# Revit family: QF_ELECTROLUXPROFESSIONAL_1LSN7T_WB6-27_E
name_source: partatom
category: Attrezzature speciali
units: mm (PartAtom-declared; Revit-internal decimal feet)

## family parameters
Basato su piano di lavoro = No
Condiviso = No
Punto di calcolo locali = No
Quota connettore circolare = Usa diametro
Sempre verticale = Sì
Taglio con vuoti quando caricato = No
Tipo di parte = Normale

## types (133) — shared parameters
Cold Water Maximum Pressure = 0.00 psi
Cold Water Minimum Pressure = 0.00 psi
Cold Water Size = 1"
Conn Conduit = Sì
Depth Actual = 1030 mm  [stored 3.37927 ft]
Electrical Remarks = 400 V/3N ph/50/60 Hz
Height Actual = 1620 mm
Hot Water Consumption = 0 GPM
Hot Water Maximum Pressure = 0.00 psi
Hot Water Minimum Pressure = 0.00 psi
Hot Water Size = 1"
Hot Water Temperature = -460 °F
Indirect Waste Size = 1"
Latent Heat Output = 0.0
Length Actual = 1050 mm
Max Overcurrent Protection = 0 A
Min Ckt Ampacity = 0 A
Modello = WB6-27
Phase = 3
Produttore = Electrolux Professional
Sensible Heat Output = 0.0
URL = www.electroluxprofessional.com
Weight = 710
Weight in Pounds = 55.1
zero-valued in all types: Cold Water Connection Height, Gas KW, Hot Water Connection Height, Indirect Waste Connection Height, Prospetto di default, Steam Pounds per Hour

## per-type parameters (varying)
| type | Descrizione | Volts | Watts |
| 9890130043 | WASHER WB6-27 270L 2DOORS RIGHT/RIGHT NO HEATING 380-415/50/60/3 2xCOMPASS PRO 3xWATER 13xLIQ. 2xDRAIN SILVER AIDO TAP A | 415 V | 6200 W |
| 9890130063 | WASHER WB6-27 270L 2DOORS RIGHT/RIGHT EL. 380-415/50/60/3 2xCOMPASS PRO 2xWATER 13xLIQ.+POWDER SILVER AIDO | 415 V | 19500 W |
| 9890130073 | WASHER WB6-27 270L 2DOORS RIGHT/RIGHT EL. 380-415/50/60/3 2xCOMPASS PRO 2xWATER 13xLIQ. SILVER TAP ALARM | 415 V | 19500 W |
| 9890130013 | WASHER WB6-27 270L 2DOORS RIGHT/RIGHT EL. 380-415/50/60/3 2xCOMPASS PRO 2xWATER 13xLIQ. SILVER AIDO IWS TAP ALARM EXP. | 415 V | 19500 W |
| 9890130023 | WASHER WB6-27 270L 2DOORS RIGHT/RIGHT EL. 380-415/50/60/3 2xCOMPASS PRO 2xWATER 13xLIQ. SILVER TAP ALARM EXP. | 415 V | 19500 W |
| 9890130083 | WASHER WB6-27 270L 2DOORS LEFT/LEFT EL. 380-415/50/60/3 COMPASS PRO 2xWATER 13xLIQ. SILVER ALARM | 415 V | 19500 W |
| 9890130093 | WASHER WB6-27 270L 2DOORS RIGHT/RIGHT EL. 380-415/50/60/3 COMPASS PRO 2xWATER 13xLIQ. SILVER TAP ALARM EXP. | 415 V | 19500 W |
| 9890130143 | WASHER WB6-27 270L 2DOORS LEFT/RIGHT EL. 380-415/50/60/3 2xCOMPASS PRO 2xWATER 13xLIQ. SILVER AIDO ALARM | 415 V | 19500 W |
| 9890130046 | WASHER WB6-27 270L 2DOORS RIGHT/RIGHT EL. 380-415/50/60/3 2xCOMPASS PRO 2xWATER 13xLIQ. SILVER AIDO IWS TAP ALARM BMP EX | 415 V | 19500 W |
| 9890130056 | WASHER WB6-27 270L 2DOORS RIGHT/RIGHT EL. 380-415/50/60/3 COMPASS PRO 2xWATER 13xLIQ.+POWDER SST IWS TAP ALARM EXP. | 415 V | 19500 W |
| 9890130103 | WASHER WB6-27 270L 2DOORS LEFT/LEFT EL. 380-415/50/60/3 COMPASS PRO 2xWATER 13xLIQ.+POWDER SILVER EXP. | 415 V | 19500 W |
| 9890130076 | WASHER WB6-27 270L 2DOORS RIGHT/RIGHT EL. 380-415/50/60/3 COMPASS PRO 2xWATER 13xLIQ. SILVER ALARM | 415 V | 19500 W |
| 9890130123 | WASHER WB6-27 270L 2DOORS LEFT/LEFT EL. 380-415/50/60/3 2xCOMPASS PRO 2xWATER 13xLIQ. SILVER | 415 V | 19500 W |
| 9890130016 | WASHER WB6-27 270L 2DOORS RIGHT/RIGHT EL. 380-415/50/60/3 2xCOMPASS PRO 2xWATER 13xLIQ. SILVER | 415 V | 19500 W |
| 9890130133 | WASHER WB6-27 270L 2DOORS RIGHT/RIGHT EL. 380-415/50/60/3 COMPASS PRO 2xWATER 13xLIQ.+POWDER SILVER TAP ALARM | 415 V | 19500 W |
| 9890130006 | WASHER WB6-27 270L 2DOORS RIGHT/RIGHT NO HEATING 380-415/50/60/3 2xCOMPASS PRO 2xWATER 13xLIQ. SILVER ALARM | 415 V | 6200 W |
| 9890130036 | WASHER WB6-27 270L 2DOORS RIGHT/RIGHT NO HEATING 380-415/50/60/3 COMPASS PRO 3xWATER 13xLIQ.+POWDER SILVER | 415 V | 6200 W |
| 9890130026 | WASHER WB6-27 270L 2DOORS RIGHT/RIGHT EL. 230/50/60/3 2xCOMPASS PRO 2xWATER 13xLIQ. SILVER AIDO TAP ALARM EXP. | 230 V | 19500 W |
| 9890130066 | WASHER WB6-27 270L 2DOORS RIGHT/RIGHT EL. 380-415/50/60/3 COMPASS PRO 3xWATER 13xLIQ. SILVER EXP. | 415 V | 19500 W |
| 9890130113 | WASHER WB6-27 270L 2DOORS RIGHT/RIGHT EL. 380-415/50/60/3 COMPASS PRO 2xWATER 13xLIQ. SILVER EXP. | 415 V | 19500 W |
| 9890130086 | WASHER WB6-27 270L 2DOORS LEFT/RIGHT EL. 380-415/50/60/3 2xCOMPASS PRO 3xWATER 13xLIQ.+POWDER SST ALARM EXP. | 415 V | 19500 W |
| 9890130096 | WASHER WB6-27 270L 2DOORS RIGHT/RIGHT EL. 380-415/50/60/3 2xCOMPASS PRO 2xWATER 13xLIQ. SST IWS | 415 V | 19500 W |
| 9890130148 | WASHER WB6-27 270L 2DOORS RIGHT/RIGHT EL. 380-415/50/60/3 COMPASS PRO 3xWATER 13xLIQ. 2xDRAIN SILVER IWS TAP ALARM | 415 V | 19500 W |
| 9890130108 | WASHER WB6-27 270L 2DOORS RIGHT/RIGHT EL. 200/60/3 COMPASS PRO 2xWATER 13xLIQ.+POWDER SST IWS ALARM EXP. | 200 V | 19500 W |
| 9890130118 | WASHER WB6-27 270L 2DOORS RIGHT/RIGHT EL. 208-240/50/60/3 2xCOMPASS PRO 2xWATER 13xLIQ. SILVER TAP ALARM EXP. | 240 V | 19500 W |
| 9890130128 | WASHER WB6-27 270L 2DOORS LEFT/RIGHT EL. 380-415/50/60/3 2xCOMPASS PRO 2xWATER 13xLIQ. SILVER TAP ALARM | 415 V | 19500 W |
| 9890130042 | WASHER WB6-27 270L 2DOORS RIGHT/RIGHT EL. 380-415/50/60/3 COMPASS PRO 2xWATER 13xLIQ.+POWDER SILVER EXP. | 415 V | 19500 W |
| 9890130052 | WASHER WB6-27 270L 2DOORS RIGHT/RIGHT EL. 380-415/50/60/3 2xCOMPASS PRO 2xWATER 13xLIQ.+POWDER SILVER EXP. | 415 V | 19500 W |
| 9890130062 | WASHER WB6-27 270L 2DOORS RIGHT/LEFT EL. 380-415/50/60/3 COMPASS PRO 3xWATER 13xLIQ.+POWDER SILVER EXP. | 415 V | 19500 W |
| 9890130012 | WASHER WB6-27 270L 2DOORS RIGHT/RIGHT EL. 380-415/50/60/3 COMPASS PRO 3xWATER 13xLIQ. SILVER IWS ALARM | 415 V | 19500 W |
| 9890130022 | WASHER WB6-27 270L 2DOORS LEFT/RIGHT EL. 380-415/50/60/3 2xCOMPASS PRO 2xWATER 13xLIQ. SILVER EXP. | 415 V | 19500 W |
| 9890130032 | WASHER WB6-27 270L 2DOORS RIGHT/RIGHT EL. 380-415/50/60/3 2xCOMPASS PRO 2xWATER 13xLIQ. SILVER ALARM | 415 V | 19500 W |
| 9890130082 | WASHER WB6-27 270L 2DOORS LEFT/RIGHT EL. 380-415/50/60/3 COMPASS PRO 2xWATER 13xLIQ. SILVER IWS | 415 V | 19500 W |
| 9890130092 | WASHER WB6-27 270L 2DOORS LEFT/RIGHT EL. 380-415/50/60/3 2xCOMPASS PRO 2xWATER 13xLIQ.+POWDER SILVER ALARM | 415 V | 19500 W |
| 9890130104 | WASHER WB6-27 270L 2DOORS RIGHT/RIGHT EL. 380-415/50/60/3 COMPASS PRO 2xWATER 13xLIQ.+POWDER SILVER EXP. | 415 V | 19500 W |
| 9890130059 | WASHER WB6-27 270L 2DOORS RIGHT/LEFT EL. 380-415/50/60/3 COMPASS PRO 2xWATER 13xLIQ. SILVER EXP. | 415 V | 19500 W |
| 9890130069 | WASHER WB6-27 270L 2DOORS RIGHT/RIGHT EL. 380-415/50/60/3 2xCOMPASS PRO 3xWATER 13xLIQ.+POWDER SILVER AIDO ALARM EXP. | 415 V | 19500 W |
| 9890130134 | WASHER WB6-27 270L 2DOORS RIGHT/RIGHT EL. 380-415/50/60/3 2xCOMPASS PRO 3xWATER 13xLIQ. SILVER AIDO ALARM | 415 V | 19500 W |
| 9890130079 | WASHER WB6-27 270L 2DOORS LEFT/LEFT EL. 380-415/50/60/3 2xCOMPASS PRO 3xWATER 13xLIQ.+POWDER 2xDRAIN SILVER TAP ALARM EX | 415 V | 19500 W |
| 9890130009 | WASHER WB6-27 270L 2DOORS RIGHT/RIGHT EL. 380-415/50/60/3 COMPASS PRO 2xWATER 13xLIQ.+POWDER SILVER EXP. | 415 V | 19500 W |
| 9890130019 | WASHER WB6-27 270L 2DOORS LEFT/RIGHT EL. 380-415/50/60/3 COMPASS PRO 2xWATER 13xLIQ. SILVER | 415 V | 19500 W |
| 9890130029 | WASHER WB6-27 270L 2DOORS RIGHT/RIGHT NO HEATING 380-415/50/60/3 COMPASS PRO 3xWATER 13xLIQ. SILVER | 415 V | 6200 W |
| 9890130039 | WASHER WB6-27 270L 2DOORS LEFT/RIGHT EL. 380-415/50/60/3 COMPASS PRO 2xWATER 13xLIQ.+POWDER SILVER | 415 V | 19500 W |
| 9890130049 | WASHER WB6-27 270L 2DOORS RIGHT/LEFT EL. 380-415/50/60/3 COMPASS PRO 2xWATER 13xLIQ.+POWDER SILVER | 415 V | 19500 W |
| 9890130114 | WASHER WB6-27 270L 2DOORS RIGHT/RIGHT EL. 380-415/50/60/3 2xCOMPASS PRO 2xWATER 13xLIQ.+POWDER SST AIDO ALARM EXP. | 415 V | 19500 W |
| 9890130089 | WASHER WB6-27 270L 2DOORS LEFT/RIGHT EL. 380-415/50/60/3 2xCOMPASS PRO 2xWATER 13xLIQ. SILVER | 415 V | 19500 W |
| 9890130099 | WASHER WB6-27 270L 2DOORS RIGHT/RIGHT EL. 380-415/50/60/3 COMPASS PRO 3xWATER 13xLIQ. SILVER TAP | 415 V | 19500 W |
| 9890130150 | WASHER WB6-27 270L 2DOORS RIGHT/RIGHT EL. 380-415/50/60/3 2xCOMPASS PRO 2xWATER 13xLIQ. SST IWS TAP ALARM BMP EXP. | 415 V | 19500 W |
| 9890130100 | WASHER WB6-27 270L 2DOORS LEFT/RIGHT NO HEATING 380-415/50/60/3 2xCOMPASS PRO 2xWATER 13xLIQ.+POWDER SILVER EXP. | 415 V | 6200 W |
| 9890130055 | WASHER WB6-27 270L 2DOORS RIGHT/RIGHT EL. 380-415/50/60/3 COMPASS PRO 3xWATER 13xLIQ.+POWDER SILVER BMP | 415 V | 19500 W |
| 9890130120 | WASHER WB6-27 270L 2DOORS RIGHT/RIGHT EL. 380-415/50/60/3 2xCOMPASS PRO 2xWATER 13xLIQ. SST AIDO ALARM | 415 V | 19500 W |
| 9890130075 | WASHER WB6-27 270L 2DOORS RIGHT/RIGHT EL. 380-415/50/60/3 2xCOMPASS PRO 2xWATER 13xLIQ. SILVER AIDO IWS ALARM | 415 V | 19500 W |
| 9890130005 | WASHER WB6-27 270L 2DOORS LEFT/RIGHT EL. 380-415/50/60/3 2xCOMPASS PRO 2xWATER 13xLIQ.+POWDER SILVER IWS TAP ALARM EXP. | 415 V | 19500 W |
| 9890130015 | WASHER WB6-27 270L 2DOORS RIGHT/RIGHT EL. 380-415/50/60/3 COMPASS PRO 2xWATER 13xLIQ. SST | 415 V | 19500 W |
| 9890130025 | WASHER WB6-27 270L 2DOORS RIGHT/RIGHT EL. 230/50/60/3 2xCOMPASS PRO 2xWATER 13xLIQ. SILVER TAP ALARM EXP. | 230 V | 19500 W |
| 9890130035 | WASHER WB6-27 270L 2DOORS RIGHT/RIGHT EL. 380-415/50/60/3 2xCOMPASS PRO 2xWATER 13xLIQ. SILVER EXP. | 415 V | 19500 W |
| 9890130110 | WASHER WB6-27 270L 2DOORS RIGHT/RIGHT NO HEATING 380-415/50/60/3 COMPASS PRO 2xWATER 13xLIQ.+POWDER SILVER EXP. | 415 V | 6200 W |
| 9890130085 | WASHER WB6-27 270L 2DOORS LEFT/RIGHT EL. 230/50/60/3 2xCOMPASS PRO 2xWATER 13xLIQ. SILVER TAP ALARM EXP. | 230 V | 19500 W |
| 9890130095 | WASHER WB6-27 270L 2DOORS RIGHT/RIGHT EL. 380-415/50/60/3 COMPASS PRO 3xWATER 13xLIQ. SILVER | 415 V | 19500 W |
| 9890130145 | WASHER WB6-27 270L 2DOORS LEFT/LEFT EL. 230/50/60/3 2xCOMPASS PRO 2xWATER 13xLIQ. SILVER TAP ALARM EXP. | 230 V | 19500 W |
| 9890130058 | WASHER WB6-27 270L 2DOORS LEFT/RIGHT EL. 380-415/50/60/3 COMPASS PRO 2xWATER 13xLIQ. SILVER EXP. | 415 V | 19500 W |
| 9890130068 | WASHER WB6-27 270L 2DOORS RIGHT/RIGHT EL. 380-415/50/60/3 2xCOMPASS PRO 2xWATER 13xLIQ. SILVER IWS TAP | 415 V | 19500 W |
| 9890130135 | WASHER WB6-27 270L 2DOORS LEFT/RIGHT EL. 380-415/50/60/3 2xCOMPASS PRO 2xWATER 13xLIQ. SILVER AIDO | 415 V | 19500 W |
| 9890130078 | WASHER WB6-27 270L 2DOORS RIGHT/RIGHT EL. 380-415/50/60/3 COMPASS PRO 2xWATER 13xLIQ. SILVER IWS | 415 V | 19500 W |
| 9890130018 | WASHER WB6-27 270L 2DOORS RIGHT/RIGHT NO HEATING 380-415/50/60/3 COMPASS PRO 3xWATER 13xLIQ. 2xDRAIN SILVER ALARM | 415 V | 6200 W |
| 9890130028 | WASHER WB6-27 270L 2DOORS RIGHT/RIGHT EL. 380-415/50/60/3 COMPASS PRO 2xWATER 13xLIQ.+POWDER SILVER ALARM | 415 V | 19500 W |
| 9890130038 | WASHER WB6-27 270L 2DOORS LEFT/LEFT EL. 380-415/50/60/3 COMPASS PRO 2xWATER 13xLIQ. SILVER IWS | 415 V | 19500 W |
| 9890130125 | WASHER WB6-27 270L 2DOORS RIGHT/LEFT EL. 380-415/50/60/3 2xCOMPASS PRO 2xWATER 13xLIQ.+POWDER SILVER ALARM EXP. | 415 V | 19500 W |
| 9890130088 | WASHER WB6-27 270L 2DOORS RIGHT/RIGHT EL. 380-415/50/60/3 2xCOMPASS PRO 2xWATER 13xLIQ. SILVER IWS ALARM BMP EXP. | 415 V | 19500 W |
| 9890130098 | WASHER WB6-27 270L 2DOORS RIGHT/RIGHT EL. 380-415/50/60/3 2xCOMPASS PRO 2xWATER 13xLIQ. SILVER IWS EXP. | 415 V | 19500 W |
| 9890130041 | WASHER WB6-27 270L 2DOORS RIGHT/RIGHT EL. 380-415/50/60/3 2xCOMPASS PRO 2xWATER 13xLIQ. SILVER AIDO ALARM BMP | 415 V | 19500 W |
| 9890130061 | WASHER WB6-27 270L 2DOORS LEFT/RIGHT EL. 380-415/50/60/3 COMPASS PRO 2xWATER 13xLIQ.+POWDER SILVER EXP. | 415 V | 19500 W |
| 9890130051 | WASHER WB6-27 270L 2DOORS RIGHT/LEFT EL. 380-415/50/60/3 COMPASS PRO 2xWATER 13xLIQ. SILVER | 415 V | 19500 W |
| 9890130011 | WASHER WB6-27 270L 2DOORS RIGHT/RIGHT EL. 380-415/50/60/3 COMPASS PRO 2xWATER 13xLIQ.+POWDER SILVER | 415 V | 19500 W |
| 9890130021 | WASHER WB6-27 270L 2DOORS RIGHT/RIGHT EL. 380-415/50/60/3 2xCOMPASS PRO 2xWATER 13xLIQ. SILVER AIDO | 415 V | 19500 W |
| 9890130031 | WASHER WB6-27 270L 2DOORS RIGHT/LEFT EL. 380-415/50/60/3 COMPASS PRO 3xWATER 13xLIQ. SILVER EXP. | 415 V | 19500 W |
| 9890130081 | WASHER WB6-27 270L 2DOORS RIGHT/LEFT EL. 380-415/50/60/3 COMPASS PRO 2xWATER 13xLIQ. SILVER IWS | 415 V | 19500 W |
| 9890130141 | WASHER WB6-27 270L 2DOORS RIGHT/RIGHT NO HEATING 380-415/50/60/3 COMPASS PRO 2xWATER 13xLIQ. SILVER | 415 V | 6200 W |
| 9890130151 | WASHER WB6-27 270L 2DOORS LEFT/RIGHT EL. 380-415/50/60/3 2xCOMPASS PRO 2xWATER 13xLIQ. SILVER TAP ALARM EXP. | 415 V | 19500 W |
| 9890130044 | WASHER WB6-27 270L 2DOORS LEFT/LEFT EL. 380-415/50/60/3 COMPASS PRO 3xWATER 13xLIQ. SILVER IWS | 415 V | 19500 W |
| 9890130054 | WASHER WB6-27 270L 2DOORS RIGHT/RIGHT EL. 380-415/50/60/3 2xCOMPASS PRO 2xWATER 13xLIQ. SILVER IWS | 415 V | 19500 W |
| 9890130064 | WASHER WB6-27 270L 2DOORS RIGHT/RIGHT EL. 380-415/50/60/3 2xCOMPASS PRO 2xWATER 13xLIQ.+POWDER SILVER ALARM EXP. | 415 V | 19500 W |
| 9890130074 | WASHER WB6-27 270L 2DOORS RIGHT/RIGHT EL. 380-415/50/60/3 2xCOMPASS PRO 2xWATER 13xLIQ.+POWDER SILVER TAP ALARM | 415 V | 19500 W |
| 9890130101 | WASHER WB6-27 270L 2DOORS LEFT/RIGHT EL. 380-415/50/60/3 COMPASS PRO 3xWATER 13xLIQ. SILVER EXP. | 415 V | 19500 W |
| 9890130014 | WASHER WB6-27 270L 2DOORS RIGHT/RIGHT NO HEATING 380-415/50/60/3 2xCOMPASS PRO 2xWATER 13xLIQ. SST ALARM | 415 V | 6200 W |
| 9890130024 | WASHER WB6-27 270L 2DOORS RIGHT/RIGHT EL. 380-415/50/60/3 2xCOMPASS PRO 2xWATER 13xLIQ. SILVER AIDO TAP ALARM EXP. | 415 V | 19500 W |
| 9890130121 | WASHER WB6-27 270L 2DOORS RIGHT/RIGHT EL. 380-415/50/60/3 2xCOMPASS PRO 2xWATER 13xLIQ.+POWDER SILVER ALARM | 415 V | 19500 W |
| 9890130004 | WASHER WB6-27 270L 2DOORS RIGHT/RIGHT EL. 380-415/50/60/3 2xCOMPASS PRO 3xWATER 13xLIQ.+POWDER SILVER IWS ALARM EXP. | 415 V | 19500 W |
| 9890130034 | WASHER WB6-27 270L 2DOORS RIGHT/RIGHT EL. 380-415/50/60/3 2xCOMPASS PRO 2xWATER 13xLIQ. SILVER AIDO ALARM | 415 V | 19500 W |
| 9893130002 | WASHER WB6-27 270L 2DOORS RIGHT/RIGHT NO HEATING 208-240/50/60/3 COMPASS PRO 2xWATER 13xLIQ.+POWDER SILVER ALARM EXP. ET | 240 V | 6200 W |
| 9890130131 | WASHER WB6-27 270L 2DOORS RIGHT/RIGHT NO HEATING 380-415/50/60/3 COMPASS PRO 2xWATER 13xLIQ. SILVER TAP ALARM EXP. | 415 V | 6200 W |
| 9890130084 | WASHER WB6-27 270L 2DOORS RIGHT/LEFT EL. 230/50/60/3 2xCOMPASS PRO 2xWATER 13xLIQ. SILVER TAP ALARM EXP. | 230 V | 19500 W |
| 9890130094 | WASHER WB6-27 270L 2DOORS RIGHT/RIGHT EL. 380-415/50/60/3 2xCOMPASS PRO 2xWATER 13xLIQ.+POWDER SILVER ALARM EXP. | 415 V | 19500 W |
| 9891130004 | WASHER WB6-27 270L 1DOOR RIGHT EL. 380-415/50/60/3 COMPASS PRO 2xWATER 13xLIQ. SILVER | 415 V | 19500 W |
| 9890130040 | WASHER WB6-27 270L 2DOORS RIGHT/LEFT EL. 380-415/50/60/3 2xCOMPASS PRO 2xWATER 13xLIQ.+POWDER SILVER | 415 V | 19500 W |
| 9890130050 | WASHER WB6-27 270L 2DOORS RIGHT/RIGHT EL. 380-415/50/60/3 2xCOMPASS PRO 2xWATER 13xLIQ.+POWDER SILVER | 415 V | 19500 W |
| 9890130070 | WASHER WB6-27 270L 2DOORS LEFT/RIGHT EL. 380-415/50/60/3 2xCOMPASS PRO 2xWATER 13xLIQ. SST IWS BMP EXP. | 415 V | 19500 W |
| 9890130010 | WASHER WB6-27 270L 2DOORS RIGHT/RIGHT EL. 380-415/50/60/3 COMPASS PRO 2xWATER 13xLIQ. SILVER | 415 V | 19500 W |
| 9890130020 | WASHER WB6-27 270L 2DOORS RIGHT/RIGHT EL. 380-415/50/60/3 COMPASS PRO 3xWATER 13xLIQ.+POWDER SILVER EXP. | 415 V | 19500 W |
| 9890130030 | WASHER WB6-27 270L 2DOORS LEFT/LEFT EL. 380-415/50/60/3 COMPASS PRO 2xWATER 13xLIQ. SILVER | 415 V | 19500 W |
| 9890130080 | WASHER WB6-27 270L 2DOORS LEFT/RIGHT EL. 380-415/50/60/3 2xCOMPASS PRO 3xWATER 13xLIQ.+POWDER 2xDRAIN SILVER AIDO TAP AL | 415 V | 19500 W |
| 9890130090 | WASHER WB6-27 270L 2DOORS RIGHT/RIGHT EL. 380-415/50/60/3 COMPASS PRO 3xWATER 13xLIQ. SILVER TAP ALARM | 415 V | 19500 W |
| 9893130003 | WASHER WB6-27 270L 2DOORS RIGHT/RIGHT EL. 208-240/50/60/3 COMPASS PRO 2xWATER 13xLIQ.+POWDER SILVER ALARM EXP. ETL | 240 V | 19500 W |
| 9891130001 | WASHER WB6-27 270L 1DOOR RIGHT EL. 380-415/50/60/3 COMPASS PRO 2xWATER 13xLIQ.+POWDER SILVER | 415 V | 19500 W |
| 9890130149 | WASHER WB6-27 270L 2DOORS RIGHT/RIGHT EL. 380-415/50/60/3 2xCOMPASS PRO 2xWATER 13xLIQ. SILVER ALARM BMP EXP. | 415 V | 19500 W |
| 9890130109 | WASHER WB6-27 270L 2DOORS LEFT/LEFT EL. 380-415/50/60/3 2xCOMPASS PRO 2xWATER 13xLIQ. SILVER IWS ALARM | 415 V | 19500 W |
| 9890130119 | WASHER WB6-27 270L 2DOORS RIGHT/RIGHT EL. 380-415/50/60/3 2xCOMPASS PRO 3xWATER 13xLIQ. 2xDRAIN SILVER ALARM | 415 V | 19500 W |
| 9890130129 | WASHER WB6-27 270L 2DOORS RIGHT/RIGHT EL. 380-415/50/60/3 2xCOMPASS PRO 3xWATER 13xLIQ.+POWDER SILVER AIDO TAP ALARM | 415 V | 19500 W |
| 9890130139 | WASHER WB6-27 270L 2DOORS LEFT/RIGHT EL. 380-415/50/60/3 COMPASS PRO 2xWATER 13xLIQ. SST EXP. | 415 V | 19500 W |
| 9891130002 | WASHER WB6-27 270L 1DOOR RIGHT EL. 380-415/50/60/3 COMPASS PRO 2xWATER 13xLIQ.+POWDER SILVER EXP. | 415 V | 19500 W |
| 9893130001 | WASHER WB6-27 270L 2DOORS RIGHT/RIGHT NO HEATING 208-240/50/60/3 COMPASS PRO 2xWATER 13xLIQ.+POWDER SST ALARM EXP. ETL | 240 V | 6200 W |
| 9890130146 | WASHER WB6-27 270L 2DOORS LEFT/RIGHT EL. 380-415/50/60/3 COMPASS PRO 3xWATER 13xLIQ. SILVER IWS ALARM | 415 V | 19500 W |
| 9890130106 | WASHER WB6-27 270L 2DOORS LEFT/RIGHT EL. 380-415/50/60/3 2xCOMPASS PRO 3xWATER 13xLIQ.+POWDER SILVER AIDO TAP ALARM EXP. | 415 V | 19500 W |
| 9890130116 | WASHER WB6-27 270L 2DOORS LEFT/RIGHT EL. 380-415/50/60/3 2xCOMPASS PRO 2xWATER 13xLIQ. SILVER IWS ALARM | 415 V | 19500 W |
| 9890130136 | WASHER WB6-27 270L 2DOORS RIGHT/LEFT EL. 380-415/50/60/3 COMPASS PRO 2xWATER 13xLIQ. SILVER ALARM | 415 V | 19500 W |
| 9891130003 | WASHER WB6-27 270L 1DOOR LEFT EL. 380-415/50/60/3 COMPASS PRO 2xWATER 13xLIQ. SILVER | 415 V | 19500 W |
| 9890130142 | WASHER WB6-27 270L 2DOORS LEFT/RIGHT EL. 380-415/50/60/3 COMPASS PRO 2xWATER 13xLIQ. SILVER ALARM EXP. | 415 V | 19500 W |
| 9890130102 | WASHER WB6-27 270L 2DOORS LEFT/RIGHT EL. 380-415/50/60/3 2xCOMPASS PRO 2xWATER 13xLIQ.+POWDER SILVER EXP. | 415 V | 19500 W |
| 9890130057 | WASHER WB6-27 270L 2DOORS RIGHT/RIGHT EL. 380-415/50/60/3 COMPASS PRO 2xWATER 13xLIQ. SST IWS TAP ALARM EXP. | 415 V | 19500 W |
| 9890130047 | WASHER WB6-27 270L 2DOORS RIGHT/LEFT EL. 380-415/50/60/3 COMPASS PRO 2xWATER 13xLIQ.+POWDER SILVER EXP. | 415 V | 19500 W |
| 9890130132 | WASHER WB6-27 270L 2DOORS RIGHT/RIGHT EL. 380-415/50/60/3 2xCOMPASS PRO 3xWATER 13xLIQ.+POWDER 2xDRAIN SILVER ALARM EXP. | 415 V | 19500 W |
| 9890130007 | WASHER WB6-27 270L 2DOORS LEFT/RIGHT EL. 380-415/50/60/3 2xCOMPASS PRO 2xWATER 13xLIQ.+POWDER SILVER AIDO IWS TAP ALARM | 415 V | 19500 W |
| 9890130017 | WASHER WB6-27 270L 2DOORS RIGHT/LEFT EL. 380-415/50/60/3 2xCOMPASS PRO 2xWATER 13xLIQ. SILVER | 415 V | 19500 W |
| 9890130027 | WASHER WB6-27 270L 2DOORS LEFT/RIGHT EL. 380-415/50/60/3 COMPASS PRO 2xWATER 13xLIQ. SILVER ALARM | 415 V | 19500 W |
| 9890130037 | WASHER WB6-27 270L 2DOORS RIGHT/RIGHT NO HEATING 380-415/50/60/3 2xCOMPASS PRO 3xWATER 13xLIQ. 2xDRAIN SILVER AIDO TAP A | 415 V | 6200 W |
| 9890130067 | WASHER WB6-27 270L 2DOORS RIGHT/RIGHT EL. 380-415/50/60/3 COMPASS PRO 2xWATER 13xLIQ.+POWDER SST IWS EXP. | 415 V | 19500 W |
| 9890130087 | WASHER WB6-27 270L 2DOORS LEFT/LEFT EL. 380-415/50/60/3 COMPASS PRO 3xWATER 13xLIQ. SILVER EXP. | 415 V | 19500 W |
| 9890130097 | WASHER WB6-27 270L 2DOORS LEFT/RIGHT EL. 380-415/50/60/3 COMPASS PRO 3xWATER 13xLIQ.+POWDER SILVER EXP. | 415 V | 19500 W |
| 9890130147 | WASHER WB6-27 270L 2DOORS RIGHT/RIGHT EL. 380-415/50/60/3 2xCOMPASS PRO 2xWATER 13xLIQ. SILVER AIDO IWS | 415 V | 19500 W |
| 9890130107 | WASHER WB6-27 270L 2DOORS RIGHT/RIGHT EL. 380-415/50/60/3 COMPASS PRO 2xWATER 13xLIQ.+POWDER SILVER ALARM EXP. | 415 V | 19500 W |
| 9890130117 | WASHER WB6-27 270L 2DOORS RIGHT/RIGHT EL. 380-415/50/60/3 2xCOMPASS PRO 3xWATER 13xLIQ.+POWDER SILVER IWS ALARM BMP EXP. | 415 V | 19500 W |
| 9890130127 | WASHER WB6-27 270L 2DOORS RIGHT/RIGHT EL. 380-415/50/60/3 COMPASS PRO 2xWATER 13xLIQ. SILVER IWS TAP EXP. | 415 V | 19500 W |
| 9890130137 | WASHER WB6-27 270L 2DOORS RIGHT/RIGHT EL. 380-415/50/60/3 2xCOMPASS PRO 3xWATER 13xLIQ. SILVER AIDO | 415 V | 19500 W |

note: [stored X ft] marks values corroborated as IEEE doubles in the binary element streams (Revit-internal decimal feet)

## geometry (parser evidence)
native form markers: Blend x14, Sweep x3
no freeform markers — native parametric forms only
